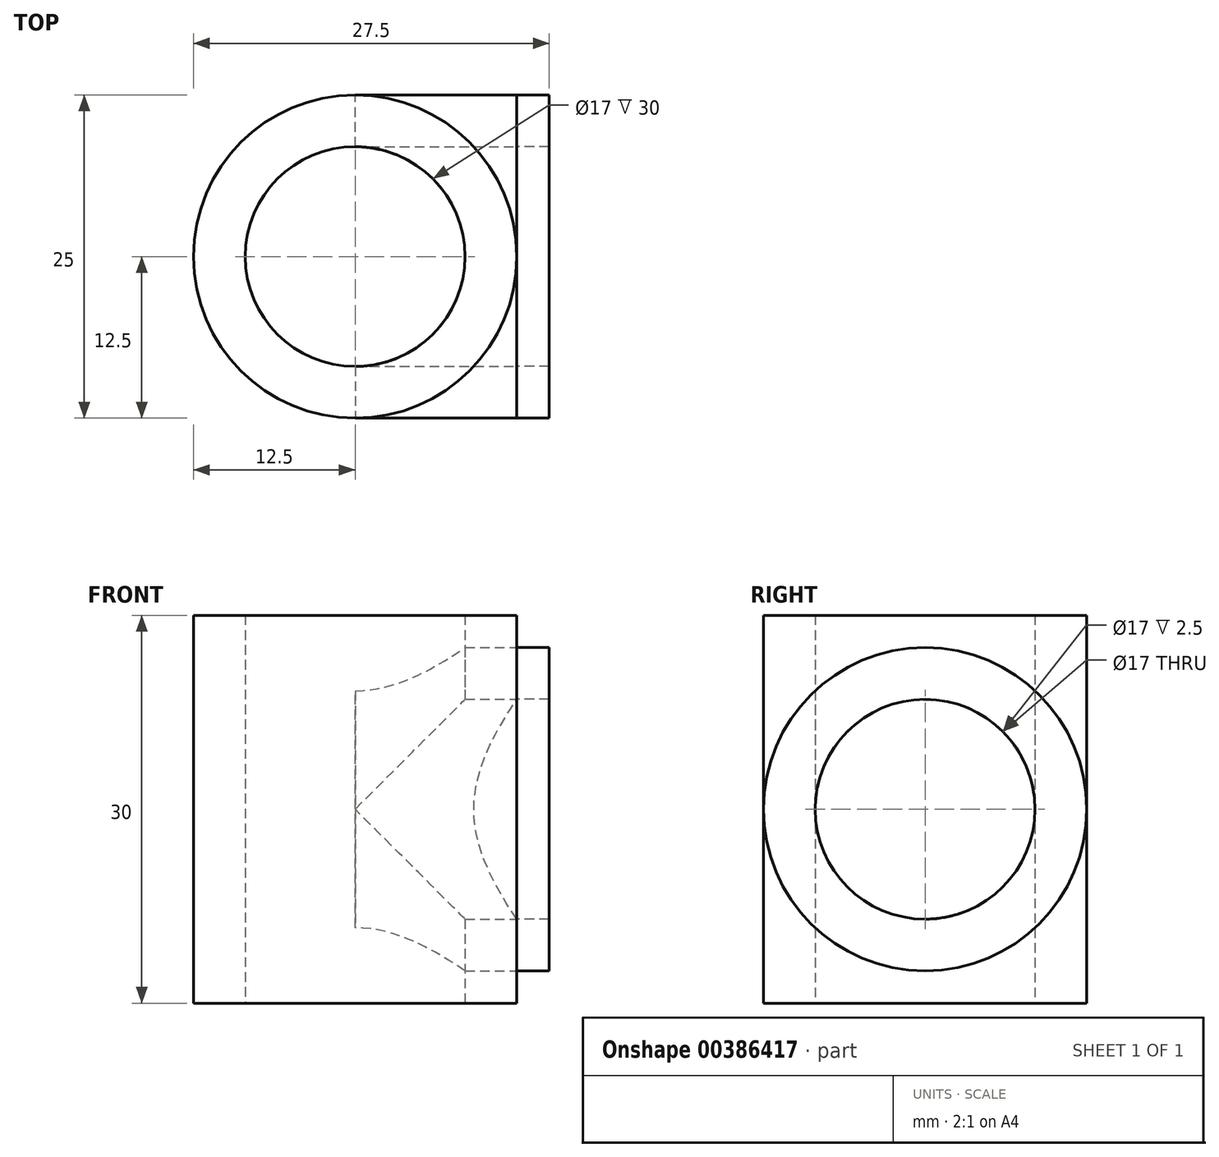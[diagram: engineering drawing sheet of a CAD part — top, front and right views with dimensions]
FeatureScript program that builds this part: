
annotation { "Feature Type Name" : "Feature", "Feature Type Description" : "" }
export const myFeature = defineFeature(function(context is Context, id is Id, definition is map)
    precondition{}
    {
        {
            var Q0;
            Q0=qCreatedBy(makeId("Top.planeOp"),FACE);
            var sketch = newSketch(context, id + "F0", { "sketchPlane" : qUnion([Q0])});
            skCircle(sketch, "E0", {"center": v(0, 0) * mm, "radius": 8.5 * mm});
            skCircle(sketch, "E1", {"center": v(0, 0) * mm, "radius": 12.5 * mm});
            skSolve(sketch);
        }
        {
            var Q0;
            Q0 = qSketchRegion(id + "F0", true);
            extrude(context, id + "F1", {"entities" : qUnion([Q0]), "depth" : 30 * mm});
        }
        {
            var Q0;
            Q0=qCreatedBy(makeId("Front.planeOp"),FACE);
            var sketch = newSketch(context, id + "F2", { "sketchPlane" : qUnion([Q0])});
            skLineSegment(sketch, "E2", {"start": v(0, 0) * mm, "end": v(0, 15) * mm});
            skLineSegment(sketch, "E3", {"start": v(0, 15) * mm, "end": v(12.5, 15) * mm});
            skSolve(sketch);
        }
        {
            var Q0;
            Q0=sQuery(id+"F2.wireOp",VERTEX,"E3.end");
            var Q1;
            Q1=sQuery(id+"F2.wireOp",EDGE,"E3");
            cPlane(context, id + "F3", {"entities" : qUnion([Q0, Q1]), "cplaneType" : CPlaneType.LINE_POINT, "offset" : 25 * mm, "width" : 150 * mm, "height" : 150 * mm});
        }
        {
            var Q0;
            Q0=qCreatedBy(id+"F3.planeOp",FACE);
            var sketch = newSketch(context, id + "F4", { "sketchPlane" : qUnion([Q0])});
            skCircle(sketch, "E4", {"center": v(0, 15) * mm, "radius": 8.5 * mm});
            skCircle(sketch, "E5", {"center": v(0, 15) * mm, "radius": 12.5 * mm});
            skSolve(sketch);
        }
        {
            var Q0;
            Q0 = qSketchRegion(id + "F4", true);
            extrude(context, id + "F5", {"entities" : qUnion([Q0]), "oppositeDirection" : true, "depth" : 12.5 * mm});
        }
        {
            var Q0;
            Q0=makeQuery(id+"F4.imprint","IMPRINT",FACE,{"disambiguationData":[TD([[makeQuery(id+"F4.imprint","IMPRINT",EDGE,{"derivedFrom":sQuery(id+"F4.wireOp",EDGE,"E4")}),1.0]])]});
            extrude(context, id + "F6", {"entities" : qUnion([Q0]), "operationType" : NewBodyOperationType.REMOVE, "oppositeDirection" : true, "depth" : 12.5 * mm});
        }
        {
            var Q0;
            Q0=makeQuery(id+"F0.imprint","IMPRINT",FACE,{"disambiguationData":[TD([[makeQuery(id+"F0.imprint","IMPRINT",EDGE,{"derivedFrom":sQuery(id+"F0.wireOp",EDGE,"E0")}),1.0]])]});
            extrude(context, id + "F7", {"entities" : qUnion([Q0]), "operationType" : NewBodyOperationType.REMOVE, "depth" : 30 * mm});
        }
        {
            var Q0;
            Q0 = qSketchRegion(id + "F4", true);
            extrude(context, id + "F8", {"entities" : qUnion([Q0]), "depth" : 2.5 * mm});
        }
    });
